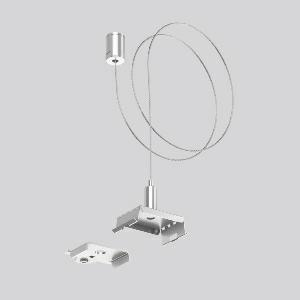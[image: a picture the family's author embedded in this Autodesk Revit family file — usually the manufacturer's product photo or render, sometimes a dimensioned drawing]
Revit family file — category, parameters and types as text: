
# Revit family: linedo_pendelset_5m_seil_982717_000_27e9
name_source: partatom
category: Lighting Fixtures
units: mm (PartAtom-declared; Revit-internal decimal feet)

## family parameters
Cut with Voids When Loaded = No
Host = Face
Light Source = No
Part Type = Normal
Room Calculation Point = No
Round Connector Dimension = Use Diameter
Shared = No

## types (1)
- LINEDO Pendelset 5m Seil
    Apparent Load = 0 VA
    Default Elevation = 1800 mm
    Description = Suspension kit with steel cable 5,000 mm. Spring steel, blank, for installing continuous line luminaire modules.
Colour: stainless steel
Weight: 185 g
Type of Installation: pendant
    Height = 326 mm
    Lamp = 0 x
    Length = 187 mm
    Luminous efficacy = 0 lm/W
    Manufacturer = RZB
    ModVariant = No
    Model = 982717.000
    Mounting Place = Ceiling
    Mounting Type = Surface mounted
    Number of Poles = 1
    OnlyDefault = Yes
    Power Factor = 1
    Product Name = LINEDO Pendelset 5m Seil
    Product group = Surface mounted continuous line luminaire system
    ProductGroupID = 310
    Protection Class = Protection class
    Protection Degree = Degree of protection
    RLX_Detail_Level = 1
    RLX_Emergency_Light_Flux = 0 lm
    RLX_Emergency_Type = 0
    RLX_Emergency_Type_DB = No
    RlxData = <blob elided: 23549 chars, md5=d51ee18d>
    Standby Power = 0 W
    System Light Flux = 0 lm
    System Power = 0 W
    Type Comments = Product without accessories
    Type Image = 982717.000.jpg
    URL = http://relux.com
    VarID = ---
    Voltage = 0 V
    Weight = 0.00 kg
    Width = 0 mm  [stored 0 ft]

note: [stored X ft] marks values corroborated as IEEE doubles in the binary element streams (Revit-internal decimal feet)

## geometry (parser evidence)
native form markers: Blend x4, Sweep x11
no freeform markers — native parametric forms only
